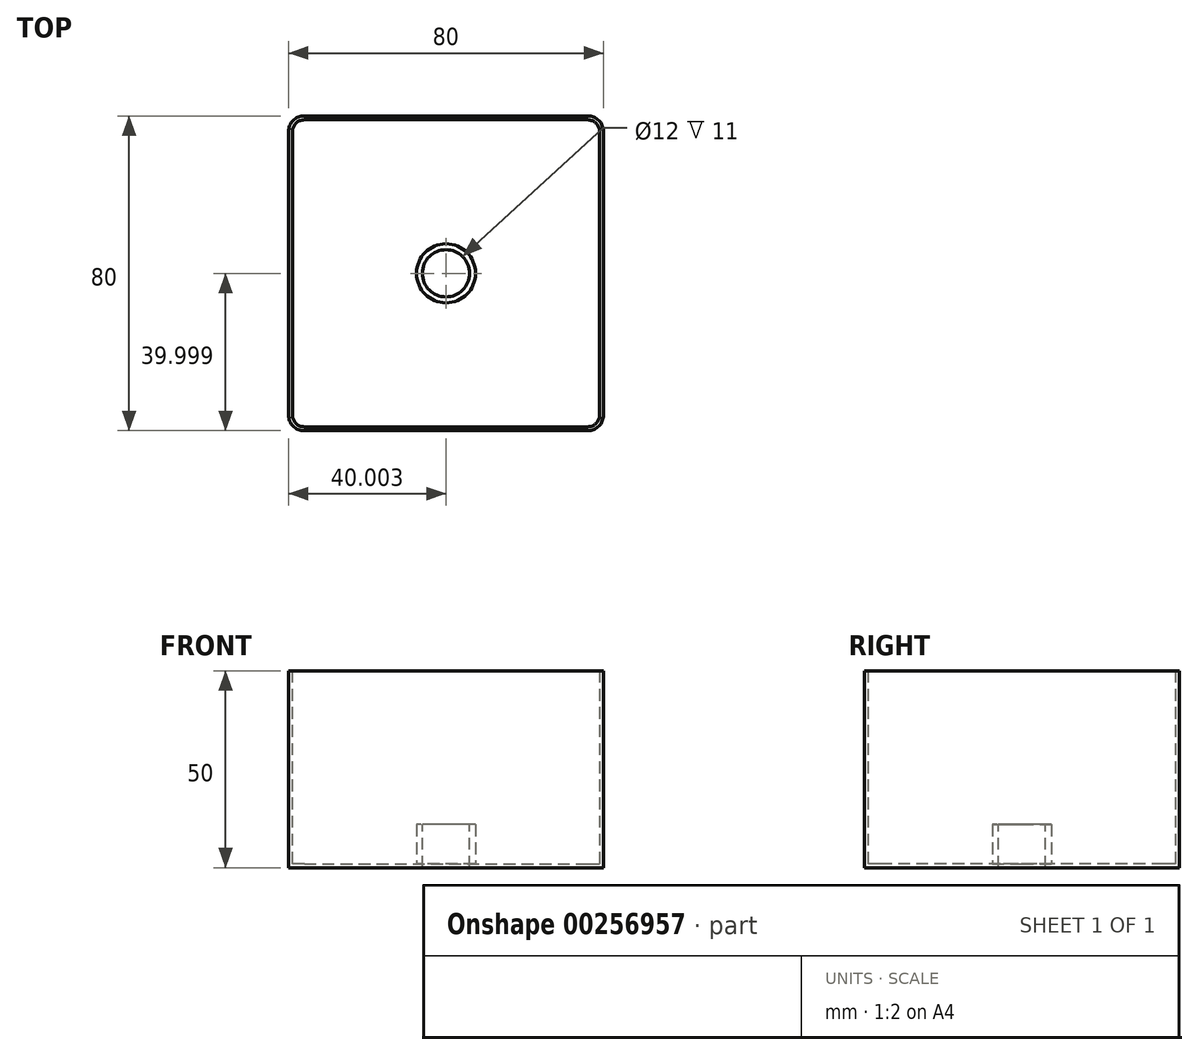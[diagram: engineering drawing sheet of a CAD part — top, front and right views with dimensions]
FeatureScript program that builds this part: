
annotation { "Feature Type Name" : "Feature", "Feature Type Description" : "" }
export const myFeature = defineFeature(function(context is Context, id is Id, definition is map)
    precondition{}
    {
        {
            var Q0;
            Q0=qCreatedBy(makeId("Top.planeOp"),FACE);
            var sketch = newSketch(context, id + "F0", { "sketchPlane" : qUnion([Q0])});
            skArc(sketch, "E0", {"start": v(-14.84, 69.63) * mm, "mid": v(-17.67, 68.46) * mm, "end": v(-18.84, 65.63) * mm});
            skLineSegment(sketch, "E1", {"start": v(-14.84, 69.63) * mm, "end": v(57.16, 69.63) * mm});
            skArc(sketch, "E2", {"start": v(61.16, 65.63) * mm, "mid": v(60, 68.46) * mm, "end": v(57.16, 69.63) * mm});
            skLineSegment(sketch, "E3", {"start": v(57.16, 65.63) * mm, "end": v(57.16, 69.63) * mm, "construction": true});
            skLineSegment(sketch, "E4", {"start": v(-14.84, 69.63) * mm, "end": v(-14.84, 65.63) * mm, "construction": true});
            skLineSegment(sketch, "E5", {"start": v(-18.84, 65.63) * mm, "end": v(-18.84, -6.37) * mm});
            skArc(sketch, "E6", {"start": v(-18.84, -6.37) * mm, "mid": v(-17.67, -9.2) * mm, "end": v(-14.84, -10.37) * mm});
            skArc(sketch, "E7", {"start": v(57.16, -10.37) * mm, "mid": v(60, -9.2) * mm, "end": v(61.16, -6.37) * mm});
            skLineSegment(sketch, "E8", {"start": v(-14.84, -10.37) * mm, "end": v(57.16, -10.37) * mm});
            skLineSegment(sketch, "E9", {"start": v(61.16, 65.63) * mm, "end": v(61.16, -6.37) * mm});
            skLineSegment(sketch, "E10", {"start": v(-14.84, -6.37) * mm, "end": v(-18.84, -6.37) * mm, "construction": true});
            skLineSegment(sketch, "E11", {"start": v(-14.84, -6.37) * mm, "end": v(-14.84, -10.37) * mm, "construction": true});
            skLineSegment(sketch, "E12", {"start": v(57.16, -6.37) * mm, "end": v(57.16, -10.37) * mm, "construction": true});
            skLineSegment(sketch, "E13", {"start": v(57.16, -10.37) * mm, "end": v(57.16, -6.37) * mm, "construction": true});
            skLineSegment(sketch, "E14", {"start": v(57.16, -6.37) * mm, "end": v(61.16, -6.37) * mm, "construction": true});
            skLineSegment(sketch, "E15", {"start": v(57.16, 65.63) * mm, "end": v(61.16, 65.63) * mm, "construction": true});
            skLineSegment(sketch, "E16", {"start": v(-18.84, 65.63) * mm, "end": v(-14.84, 65.63) * mm, "construction": true});
            skSolve(sketch);
        }
        {
            var Q0;
            Q0=makeQuery(id+"F0.imprint","IMPRINT",FACE,{"disambiguationData":[TD([[makeQuery(id+"F0.imprint","IMPRINT",EDGE,{"derivedFrom":sQuery(id+"F0.wireOp",EDGE,"E0")}),1.0]])]});
            extrude(context, id + "F1", {"entities" : qUnion([Q0]), "depth" : 50 * mm});
        }
        {
            var Q0;
            Q0=makeQuery(id+"F1.opExtrude","CAP_FACE",FACE,{"disambiguationData":[OSD([sQuery(id+"F0.wireOp",EDGE,"E0"),sQuery(id+"F0.wireOp",EDGE,"E1"),sQuery(id+"F0.wireOp",EDGE,"E2"),sQuery(id+"F0.wireOp",EDGE,"E5"),sQuery(id+"F0.wireOp",EDGE,"E6"),sQuery(id+"F0.wireOp",EDGE,"E7"),sQuery(id+"F0.wireOp",EDGE,"E8"),sQuery(id+"F0.wireOp",EDGE,"E9")])],"isStart":false});
            shell(context, id + "F2", {"entities" : qUnion([Q0]), "thickness" : 1 * mm});
        }
        {
            var Q0;
            Q0=makeQuery(id+"F2.opShell","OFFSET_FACE",FACE,{"disambiguationData":[OSD([sQuery(id+"F0.wireOp",EDGE,"E0"),sQuery(id+"F0.wireOp",EDGE,"E1"),sQuery(id+"F0.wireOp",EDGE,"E2"),sQuery(id+"F0.wireOp",EDGE,"E5"),sQuery(id+"F0.wireOp",EDGE,"E6"),sQuery(id+"F0.wireOp",EDGE,"E7"),sQuery(id+"F0.wireOp",EDGE,"E8"),sQuery(id+"F0.wireOp",EDGE,"E9")])]});
            var sketch = newSketch(context, id + "F3", { "sketchPlane" : qUnion([Q0])});
            skLineSegment(sketch, "E17", {"start": v(20.16, 68.63) * mm, "end": v(20.16, -9.37) * mm, "construction": true});
            skPoint(sketch, "E17.endSnap0", {"position": v(21.16, -9.37) * mm});
            skLineSegment(sketch, "E18", {"start": v(-17.84, 29.63) * mm, "end": v(60.16, 29.63) * mm, "construction": true});
            skCircle(sketch, "E19", {"center": v(21.16, 29.63) * mm, "radius": 6 * mm});
            skCircle(sketch, "E20", {"center": v(21.16, 29.63) * mm, "radius": 7.5 * mm});
            skSolve(sketch);
        }
        {
            var Q0;
            Q0=makeQuery(id+"F3.imprint","IMPRINT",FACE,{"disambiguationData":[TD([[makeQuery(id+"F3.imprint","IMPRINT",EDGE,{"derivedFrom":sQuery(id+"F3.wireOp",EDGE,"E19")}),1.0]])]});
            extrude(context, id + "F4", {"entities" : qUnion([Q0]), "operationType" : NewBodyOperationType.REMOVE, "endBound" : BoundingType.UP_TO_NEXT, "oppositeDirection" : true, "depth" : 25 * mm});
        }
        {
            var Q0;
            Q0=makeQuery(id+"F3.imprint","IMPRINT",FACE,{"disambiguationData":[TD([[makeQuery(id+"F3.imprint","IMPRINT",EDGE,{"derivedFrom":sQuery(id+"F3.wireOp",EDGE,"E20")}),-1.0]])]});
            cPlane(context, id + "F5", {"entities" : qUnion([Q0]), "cplaneType" : CPlaneType.OFFSET, "offset" : 10 * mm, "width" : 150 * mm, "height" : 150 * mm});
        }
        {
            var Q0;
            Q0=makeQuery(id+"F3.imprint","IMPRINT",FACE,{"disambiguationData":[TD([[makeQuery(id+"F3.imprint","IMPRINT",EDGE,{"derivedFrom":sQuery(id+"F3.wireOp",EDGE,"E19")}),-1.0]])]});
            extrude(context, id + "F6", {"entities" : qUnion([Q0]), "operationType" : NewBodyOperationType.ADD, "depth" : 10 * mm});
        }
    });
